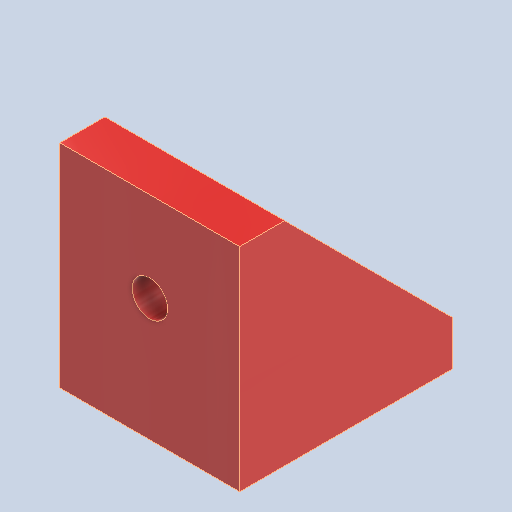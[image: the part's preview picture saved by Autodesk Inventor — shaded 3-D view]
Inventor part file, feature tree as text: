
AUTODESK INVENTOR PART (.ipt)
format: ipt  version: 2023 (Build 270158000, 158)  size: 263,680 bytes
history: native  units: in
note: dims shown in document units (in); Inventor stores cm internally (conversion verified against a paired STEP export)
features: extrude x5, sketch x5, chamfer x3, projected_geometry x2
ambient origin geometry x8: Origin, YZ Plane, XZ Plane, XY Plane, X Axis, Y Axis, Z Axis, Center Point
bodies: Solid1 (feature_tree)
feature tree (15):
  extrude  "Extrusion1"  Depth=1.1811in
  extrude  "Extrusion2"  Depth=0.25in
  extrude  "Extrusion3"  Depth=1.0in
  extrude  "Extrusion4"  Depth=0.5in
  extrude  "Extrusion5"  Depth=0.125in
  chamfer  "Chamfer1"  Distance=0.5in
  chamfer  "Chamfer2"  Distance=0.5in
  chamfer  "Chamfer3"  [1 undecoded]
  sketch  "Sketch1"  dims[d0=1.1811in d1=1.1811in]
  sketch  "Sketch2"  dims[d2=0.25in d3=0.25in]
  sketch  "Sketch3"  dims[d4=1.0in d5=0.0in d6=0.1969in]
  sketch  "Sketch4"  dims[d7=0.5in d8=0.5in]
  projected_geometry  "Projected Loop1"
  sketch  "Sketch5"  dims[d9=0.0in d10=0.0in d11=0.1969in d12=0.5in d13=0.5in d14=0.0in d15=0.0in d16=0.125in d17=1.0in d18=0.0in d19=1.0in d20=0.0in d21=0.1939in d22=0.125in d23=45.0deg d24=0.193in d25=0.125in d26=45.0deg d27=0.193in d28=0.125in d29=45.0deg]
  projected_geometry  "Projected Loop2"
note: 1 required parameter value undecoded (feature->parameter linkage not recoverable at this tier; creation-order binding heuristic only, values carry confidence <= 0.55)
